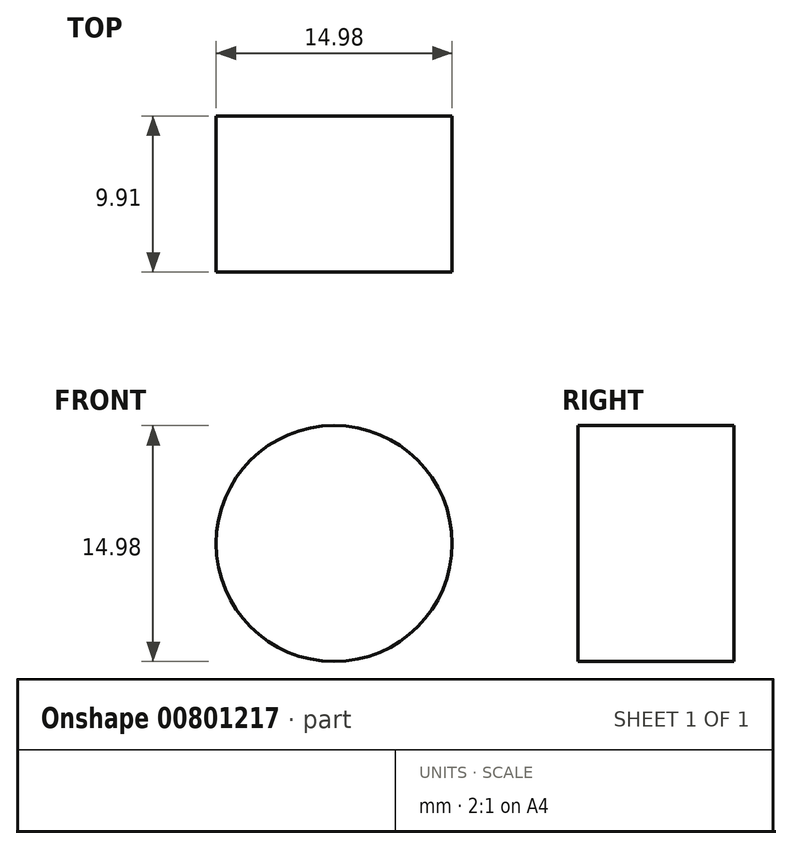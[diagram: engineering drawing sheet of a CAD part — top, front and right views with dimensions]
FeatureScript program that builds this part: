
annotation { "Feature Type Name" : "Feature", "Feature Type Description" : "" }
export const myFeature = defineFeature(function(context is Context, id is Id, definition is map)
    precondition{}
    {
        {
            var Q0;
            Q0=qCreatedBy(makeId("Front.planeOp"),FACE);
            var sketch = newSketch(context, id + "F0", { "sketchPlane" : qUnion([Q0])});
            skCircle(sketch, "E0", {"center": v(0, 0) * mm, "radius": 7.5 * mm});
            skSolve(sketch);
        }
        {
            var Q0;
            Q0 = qSketchRegion(id + "F0", true);
            extrude(context, id + "F1", {"entities" : qUnion([Q0]), "depth" : 9.9 * mm, "offsetDistance" : 25.4 * mm});
        }
    });
